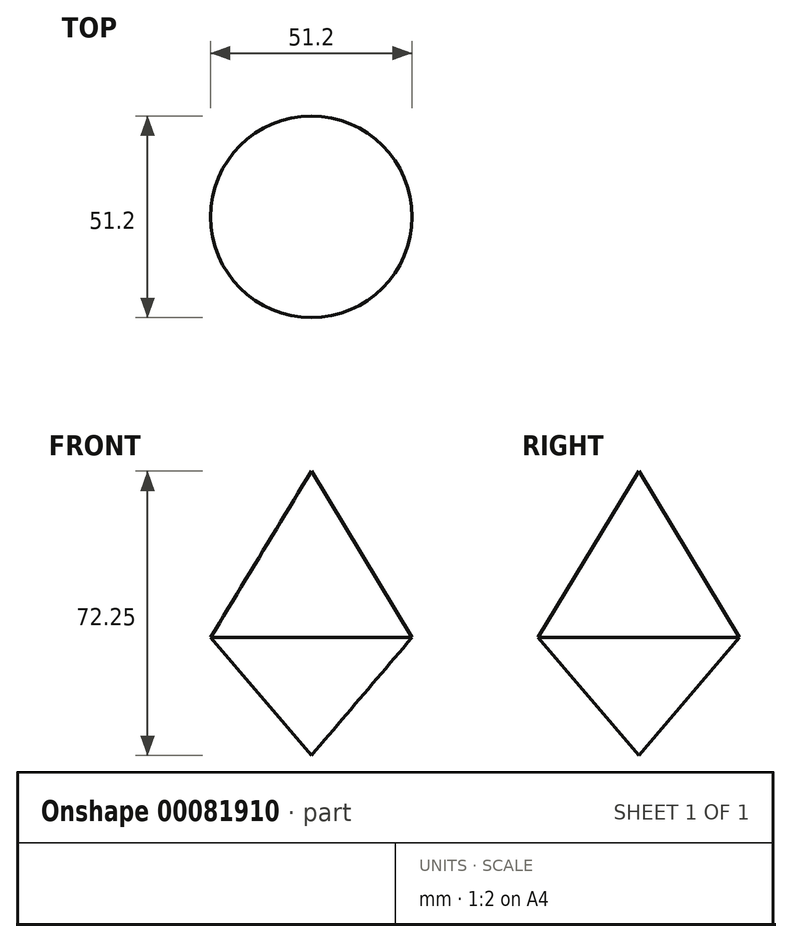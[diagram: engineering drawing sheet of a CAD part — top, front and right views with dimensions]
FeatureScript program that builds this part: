
annotation { "Feature Type Name" : "Feature", "Feature Type Description" : "" }
export const myFeature = defineFeature(function(context is Context, id is Id, definition is map)
    precondition{}
    {
        {
            var Q0;
            Q0=qCreatedBy(makeId("Front.planeOp"),FACE);
            var sketch = newSketch(context, id + "F0", { "sketchPlane" : qUnion([Q0])});
            skLineSegment(sketch, "E0", {"start": v(0, 42.28) * mm, "end": v(-25.6, 0) * mm});
            skLineSegment(sketch, "E1", {"start": v(-25.6, 0) * mm, "end": v(0, -29.97) * mm});
            skLineSegment(sketch, "E2", {"start": v(0, -29.97) * mm, "end": v(0, 42.28) * mm});
            skLineSegment(sketch, "E3", {"start": v(0, 63.34) * mm, "end": v(0, -56.86) * mm});
            skSolve(sketch);
        }
        {
            var Q0;
            {var subQ0=sQuery(id+"F0.wireOp",EDGE,"E0");Q0=makeQuery(id+"F0.imprint","IMPRINT",FACE,{"disambiguationData":[TD([[makeQuery(id+"F0.imprint","IMPRINT",EDGE,{"derivedFrom":subQ0}),1.0]])]});}
            var Q1;
            Q1=sQuery(id+"F0.wireOp",EDGE,"E3");
            revolve(context, id + "F1", {"entities" : qUnion([Q0]), "axis" : qUnion([Q1]), "revolveType" : RevolveType.FULL});
        }
    });
